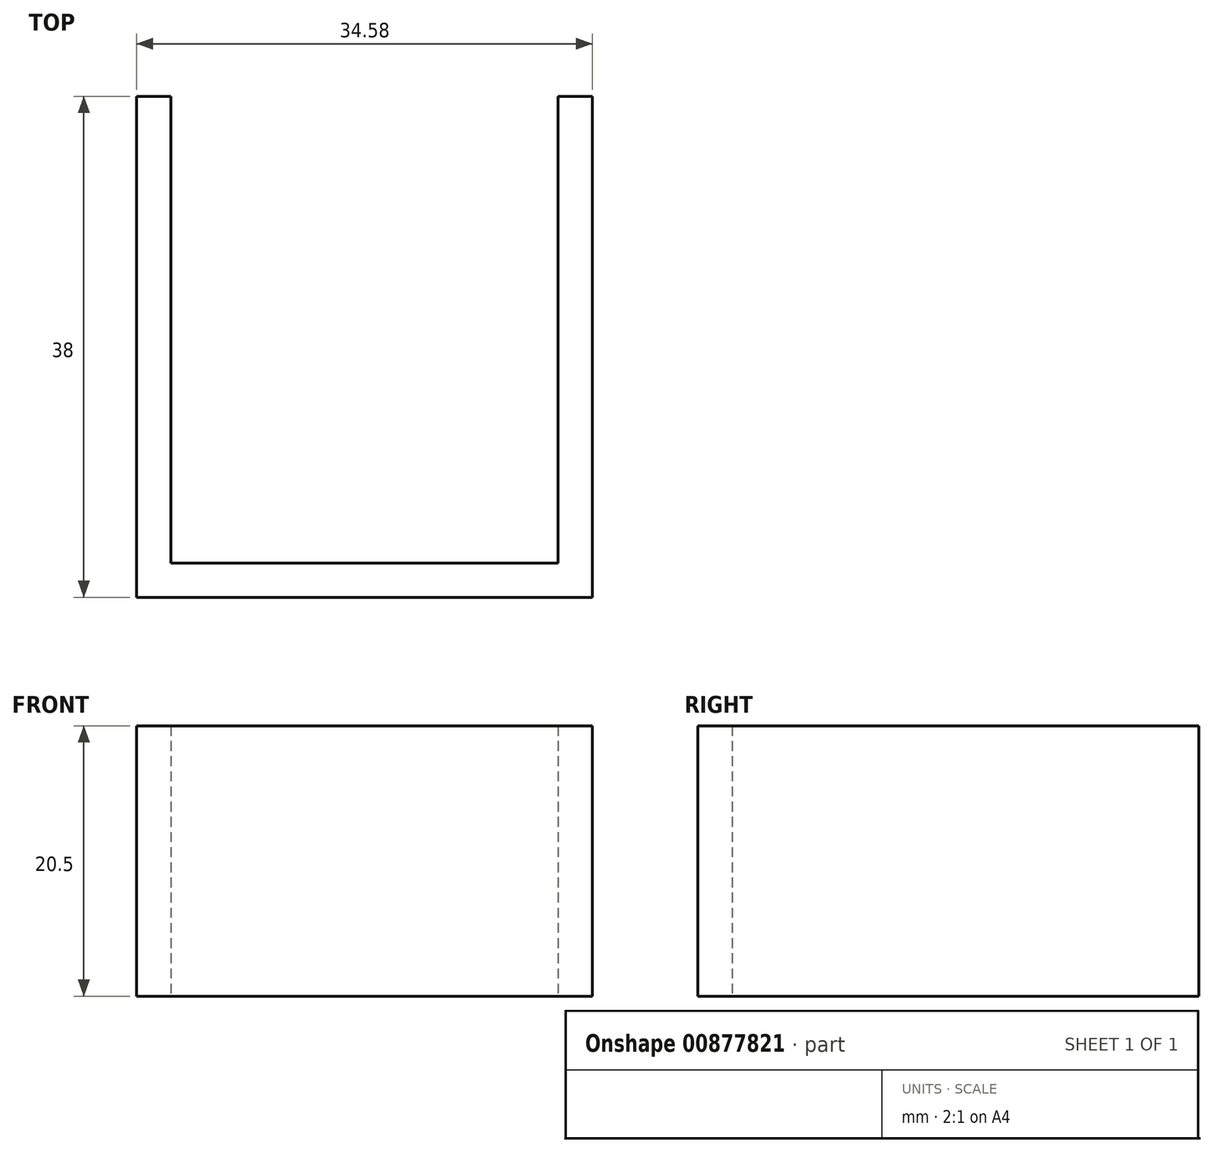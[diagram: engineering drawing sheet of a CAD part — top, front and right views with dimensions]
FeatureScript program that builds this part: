
annotation { "Feature Type Name" : "Feature", "Feature Type Description" : "" }
export const myFeature = defineFeature(function(context is Context, id is Id, definition is map)
    precondition{}
    {
        {
            var Q0;
            Q0=qCreatedBy(makeId("Top.planeOp"),FACE);
            var sketch = newSketch(context, id + "F0", { "sketchPlane" : qUnion([Q0])});
            skLineSegment(sketch, "E0.bottom", {"start": v(17.29, -19) * mm, "end": v(-17.3, -19) * mm});
            skLineSegment(sketch, "E0.top", {"start": v(17.29, 19) * mm, "end": v(-17.29, 19) * mm});
            skLineSegment(sketch, "E0.left", {"start": v(17.29, -19) * mm, "end": v(17.29, 19) * mm});
            skLineSegment(sketch, "E0.right", {"start": v(-17.29, -19) * mm, "end": v(-17.29, 19) * mm});
            skPoint(sketch, "E0.middle", {"position": v(0, 0) * mm});
            skLineSegment(sketch, "E1", {"start": v(-14.7, 19) * mm, "end": v(-14.69, -19) * mm});
            skLineSegment(sketch, "E2", {"start": v(14.69, 19) * mm, "end": v(14.69, -19) * mm});
            skLineSegment(sketch, "E3", {"start": v(-17.29, -16.4) * mm, "end": v(17.29, -16.4) * mm});
            skSolve(sketch);
        }
        {
            var Q0;
            {var subQ0=sQuery(id+"F0.wireOp",EDGE,"E0.left");var subQ1=sQuery(id+"F0.wireOp",EDGE,"E0.bottom");var subQ2=makeQuery(id+"F0.imprint","INTERSECT",VERTEX,{"derivedFrom":[subQ1,subQ0]});Q0=makeQuery(id+"F0.imprint","IMPRINT",FACE,{"disambiguationData":[TD([[makeQuery(id+"F0.imprint","IMPRINT",EDGE,{"disambiguationData":[TD([[subQ2,-1.0]])],"derivedFrom":subQ1}),-1.0]])]});}
            var Q1;
            {var subQ0=sQuery(id+"F0.wireOp",EDGE,"E0.right");var subQ1=sQuery(id+"F0.wireOp",EDGE,"E0.bottom");var subQ2=makeQuery(id+"F0.imprint","INTERSECT",VERTEX,{"derivedFrom":[subQ1,subQ0]});Q1=makeQuery(id+"F0.imprint","IMPRINT",FACE,{"disambiguationData":[TD([[makeQuery(id+"F0.imprint","IMPRINT",EDGE,{"disambiguationData":[TD([[subQ2,1.0]])],"derivedFrom":subQ1}),-1.0]])]});}
            var Q2;
            {var subQ0=sQuery(id+"F0.wireOp",EDGE,"E0.left");var subQ1=sQuery(id+"F0.wireOp",EDGE,"E0.top");var subQ2=makeQuery(id+"F0.imprint","INTERSECT",VERTEX,{"derivedFrom":[subQ1,subQ0]});Q2=makeQuery(id+"F0.imprint","IMPRINT",FACE,{"disambiguationData":[TD([[makeQuery(id+"F0.imprint","IMPRINT",EDGE,{"disambiguationData":[TD([[subQ2,-1.0]])],"derivedFrom":subQ1}),1.0]])]});}
            var Q3;
            {var subQ0=sQuery(id+"F0.wireOp",EDGE,"E0.right");var subQ1=sQuery(id+"F0.wireOp",EDGE,"E0.top");var subQ2=makeQuery(id+"F0.imprint","INTERSECT",VERTEX,{"derivedFrom":[subQ1,subQ0]});Q3=makeQuery(id+"F0.imprint","IMPRINT",FACE,{"disambiguationData":[TD([[makeQuery(id+"F0.imprint","IMPRINT",EDGE,{"disambiguationData":[TD([[subQ2,1.0]])],"derivedFrom":subQ1}),1.0]])]});}
            var Q4;
            {var subQ0=sQuery(id+"F0.wireOp",EDGE,"E1");var subQ1=sQuery(id+"F0.wireOp",EDGE,"E0.bottom");var subQ2=makeQuery(id+"F0.imprint","INTERSECT",VERTEX,{"derivedFrom":[subQ1,subQ0]});Q4=makeQuery(id+"F0.imprint","IMPRINT",FACE,{"disambiguationData":[TD([[makeQuery(id+"F0.imprint","IMPRINT",EDGE,{"disambiguationData":[TD([[subQ2,1.0]])],"derivedFrom":subQ1}),-1.0]])]});}
            extrude(context, id + "F1", {"entities" : qUnion([Q0, Q1, Q2, Q3, Q4]), "depth" : 20.5 * mm, "offsetDistance" : 25 * mm});
        }
    });
